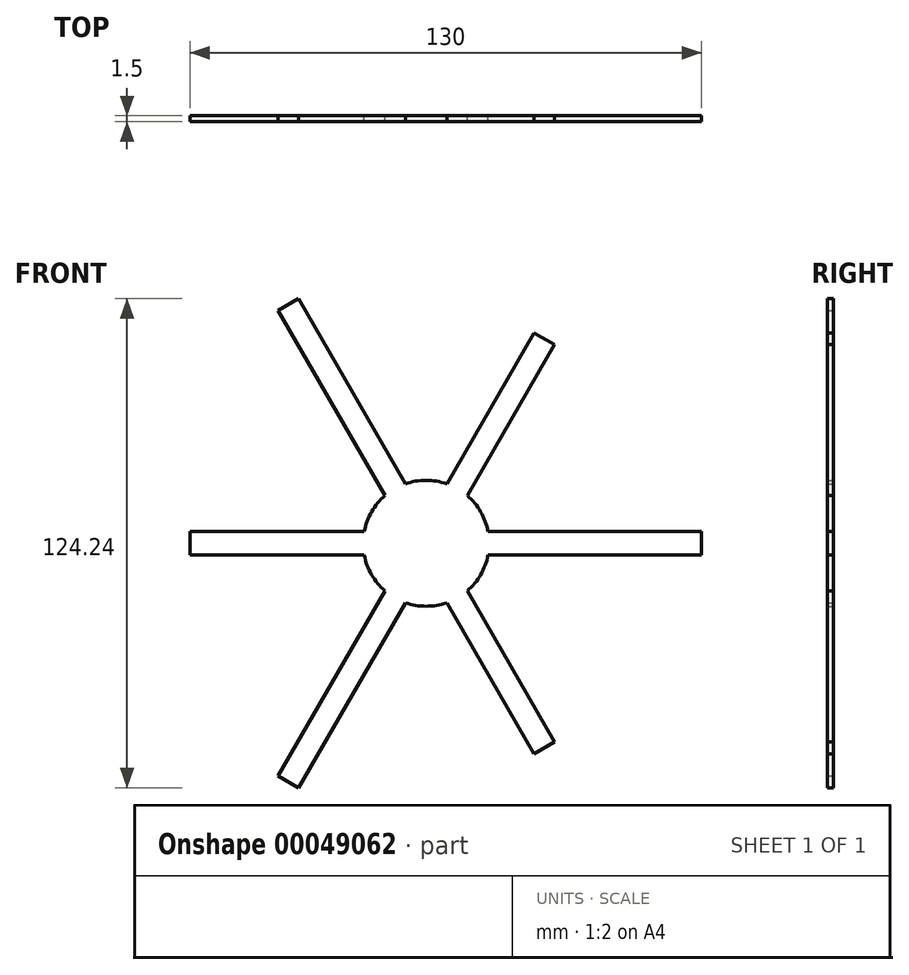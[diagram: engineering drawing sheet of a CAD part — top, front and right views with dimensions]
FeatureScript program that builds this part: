
annotation { "Feature Type Name" : "Feature", "Feature Type Description" : "" }
export const myFeature = defineFeature(function(context is Context, id is Id, definition is map)
    precondition{}
    {
        {
            var Q0;
            Q0=qCreatedBy(makeId("Front.planeOp"),FACE);
            var sketch = newSketch(context, id + "F0", { "sketchPlane" : qUnion([Q0])});
            skArc(sketch, "E0", {"start": v(-15.72, -3) * mm, "mid": v(-13.86, -8) * mm, "end": v(-10.46, -12.11) * mm});
            skLineSegment(sketch, "E1.bottom", {"start": v(70, 3) * mm, "end": v(15.72, 3) * mm});
            skLineSegment(sketch, "E1.top", {"start": v(70, -3) * mm, "end": v(15.72, -3) * mm});
            skLineSegment(sketch, "E1.left", {"start": v(70, 3) * mm, "end": v(70, -3) * mm});
            skLineSegment(sketch, "E2.1.0", {"start": v(-37.6, 59.12) * mm, "end": v(-32.4, 62.12) * mm});
            skLineSegment(sketch, "E2.1.1", {"start": v(-32.4, 62.12) * mm, "end": v(-5.26, 15.11) * mm});
            skLineSegment(sketch, "E2.1.2", {"start": v(-37.6, 59.12) * mm, "end": v(-10.46, 12.11) * mm});
            skLineSegment(sketch, "E2.2.0", {"start": v(-32.4, -62.12) * mm, "end": v(-37.6, -59.12) * mm});
            skLineSegment(sketch, "E2.2.1", {"start": v(-37.6, -59.12) * mm, "end": v(-10.46, -12.11) * mm});
            skLineSegment(sketch, "E2.2.2", {"start": v(-32.4, -62.12) * mm, "end": v(-5.26, -15.11) * mm});
            skLineSegment(sketch, "E3.bottom", {"start": v(-60, 3) * mm, "end": v(-15.72, 3) * mm});
            skLineSegment(sketch, "E3.top", {"start": v(-60, -3) * mm, "end": v(-15.72, -3) * mm});
            skLineSegment(sketch, "E3.left", {"start": v(-60, 3) * mm, "end": v(-60, -3) * mm});
            skLineSegment(sketch, "E4.1.1", {"start": v(32.6, -50.46) * mm, "end": v(10.46, -12.11) * mm});
            skLineSegment(sketch, "E4.1.2", {"start": v(27.4, -53.46) * mm, "end": v(32.6, -50.46) * mm});
            skLineSegment(sketch, "E4.1.3", {"start": v(27.4, -53.46) * mm, "end": v(5.26, -15.11) * mm});
            skLineSegment(sketch, "E4.2.1", {"start": v(27.4, 53.46) * mm, "end": v(5.26, 15.11) * mm});
            skLineSegment(sketch, "E4.2.2", {"start": v(32.6, 50.46) * mm, "end": v(27.4, 53.46) * mm});
            skLineSegment(sketch, "E4.2.3", {"start": v(32.6, 50.46) * mm, "end": v(10.46, 12.11) * mm});
            skArc(sketch, "E5.trimOffspring", {"start": v(-10.46, 12.11) * mm, "mid": v(-13.86, 8) * mm, "end": v(-15.72, 3) * mm});
            skArc(sketch, "E6.trimOffspring", {"start": v(5.26, 15.11) * mm, "mid": v(0, 16) * mm, "end": v(-5.26, 15.11) * mm});
            skArc(sketch, "E7.trimOffspring", {"start": v(15.72, 3) * mm, "mid": v(13.86, 8) * mm, "end": v(10.46, 12.11) * mm});
            skArc(sketch, "E8.trimOffspring", {"start": v(10.46, -12.11) * mm, "mid": v(13.86, -8) * mm, "end": v(15.72, -3) * mm});
            skArc(sketch, "E9.trimOffspring", {"start": v(-5.26, -15.11) * mm, "mid": v(0, -16) * mm, "end": v(5.26, -15.11) * mm});
            skSolve(sketch);
        }
        {
            var Q0;
            Q0=makeQuery(id+"F0.imprint","IMPRINT",FACE,{"disambiguationData":[TD([[makeQuery(id+"F0.imprint","IMPRINT",EDGE,{"derivedFrom":sQuery(id+"F0.wireOp",EDGE,"E0")}),1.0]])]});
            extrude(context, id + "F1", {"entities" : qUnion([Q0]), "depth" : 1.5 * mm});
        }
    });
